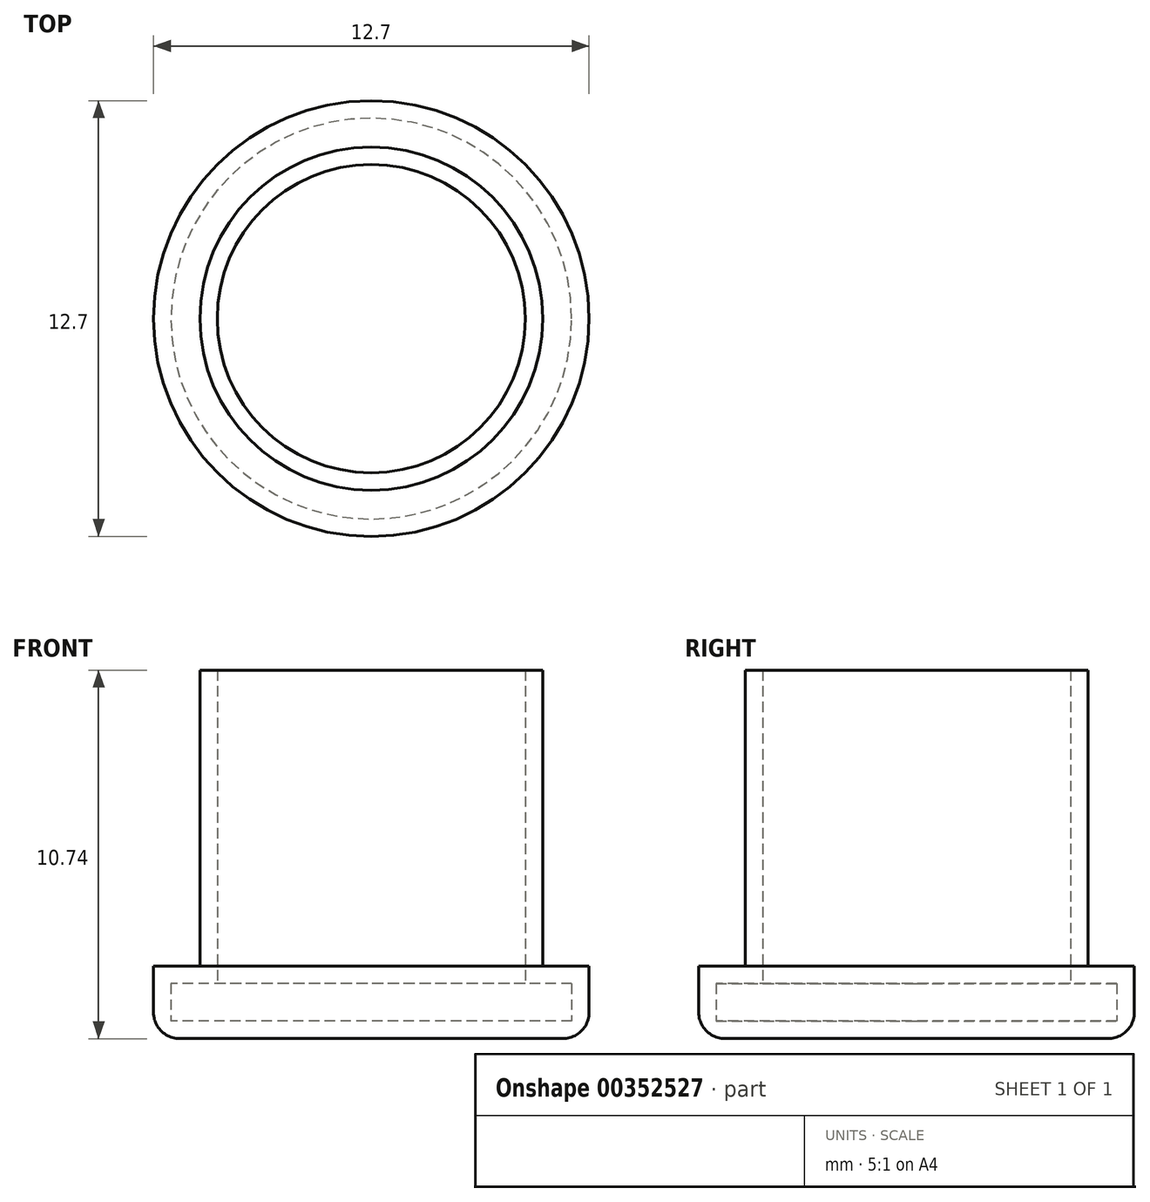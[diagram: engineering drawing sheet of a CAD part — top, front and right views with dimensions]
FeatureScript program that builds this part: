
annotation { "Feature Type Name" : "Feature", "Feature Type Description" : "" }
export const myFeature = defineFeature(function(context is Context, id is Id, definition is map)
    precondition{}
    {
        {
            var Q0;
            Q0=qCreatedBy(makeId("Top.planeOp"),FACE);
            var sketch = newSketch(context, id + "F0", { "sketchPlane" : qUnion([Q0])});
            skCircle(sketch, "E0", {"center": v(0, 0) * mm, "radius": 5 * mm});
            skCircle(sketch, "E1", {"center": v(0, 0) * mm, "radius": 6.35 * mm});
            skSolve(sketch);
        }
        {
            var Q0;
            Q0=makeQuery(id+"F0.imprint","IMPRINT",FACE,{"disambiguationData":[TD([[makeQuery(id+"F0.imprint","IMPRINT",EDGE,{"derivedFrom":sQuery(id+"F0.wireOp",EDGE,"E0")}),1.0]])]});
            var Q1;
            Q1=sQuery(id+"F0.wireOp",EDGE,"E0");
            extrude(context, id + "F1", {"entities" : qUnion([Q0]), "surfaceEntities" : qUnion([Q1]), "depth" : 10 * mm});
        }
        {
            var Q0;
            Q0=makeQuery(id+"F0.imprint","IMPRINT",FACE,{"disambiguationData":[TD([[makeQuery(id+"F0.imprint","IMPRINT",EDGE,{"derivedFrom":sQuery(id+"F0.wireOp",EDGE,"E0")}),-1.0]])]});
            var Q1;
            Q1=makeQuery(id+"F0.imprint","IMPRINT",FACE,{"disambiguationData":[TD([[makeQuery(id+"F0.imprint","IMPRINT",EDGE,{"derivedFrom":sQuery(id+"F0.wireOp",EDGE,"E0")}),1.0]])]});
            extrude(context, id + "F2", {"entities" : qUnion([Q0, Q1]), "operationType" : NewBodyOperationType.ADD, "depth" : 1.37 * mm, "hasSecondDirection" : true, "secondDirectionOppositeDirection" : true, "secondDirectionDepth" : 0.74 * mm});
        }
        {
            var Q0;
            Q0=makeQuery(id+"F1.opExtrude","CAP_FACE",FACE,{"disambiguationData":[OSD([sQuery(id+"F0.wireOp",EDGE,"E0")])],"isStart":false});
            shell(context, id + "F3", {"entities" : qUnion([Q0]), "thickness" : 0.5 * mm});
        }
        {
            var Q0;
            Q0=makeQuery(id+"F2.opExtrude","CAP_FACE",FACE,{"disambiguationData":[OSD([sQuery(id+"F0.wireOp",EDGE,"E1")])],"isStart":true});
            fillet(context, id + "F4", {"entities" : qUnion([Q0]), "radius" : 0.76 * mm, "tangentPropagation" : true, "allowEdgeOverflow" : false});
        }
    });
